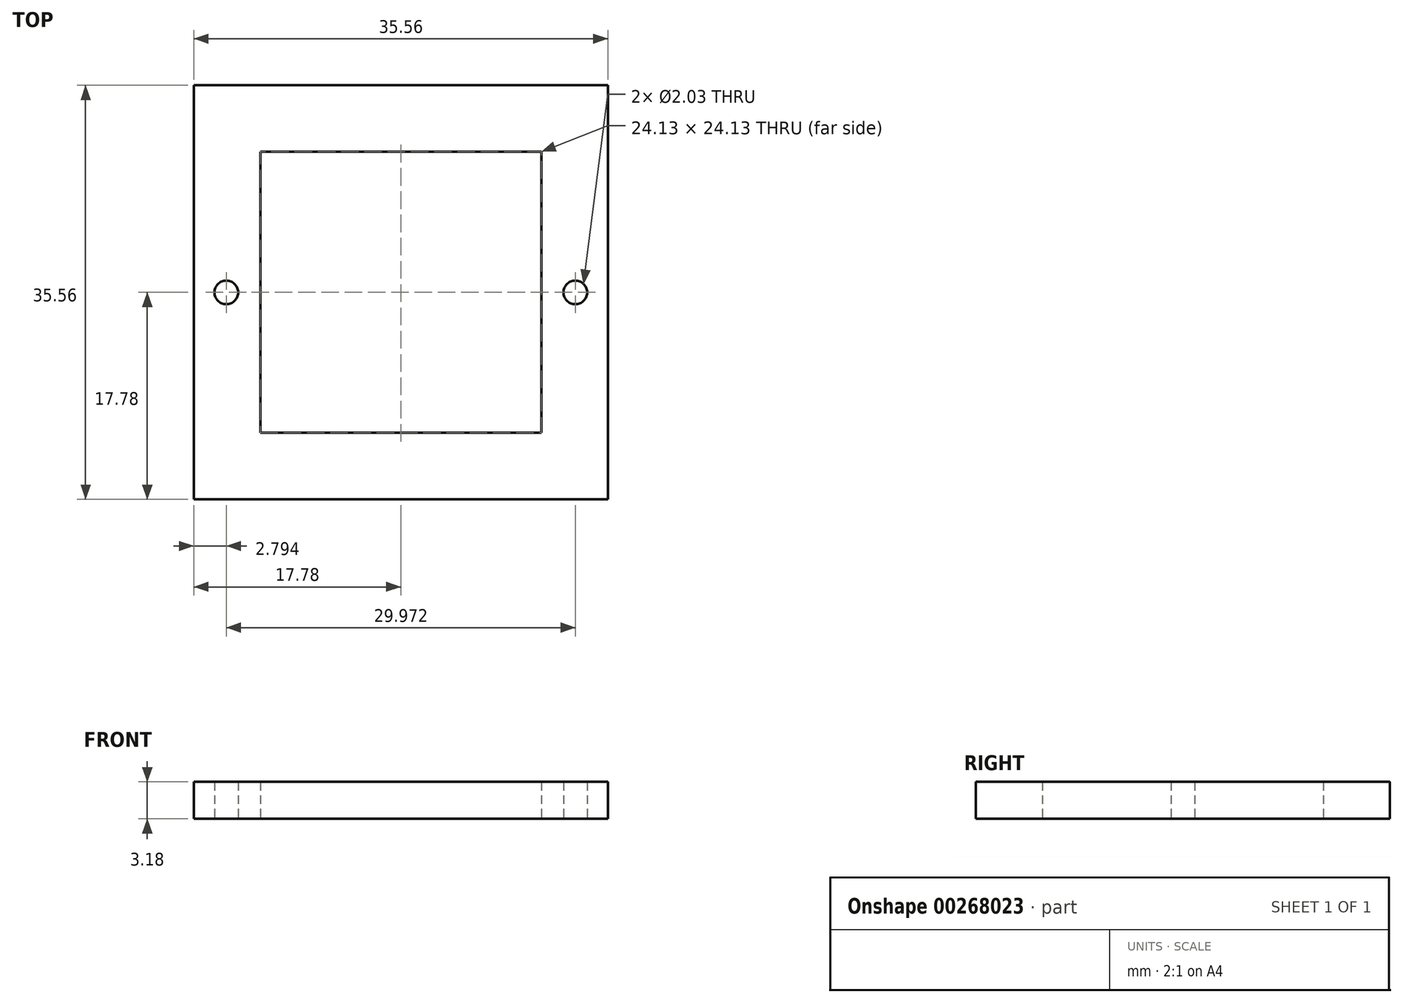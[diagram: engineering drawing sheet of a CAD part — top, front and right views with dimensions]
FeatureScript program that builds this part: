
annotation { "Feature Type Name" : "Feature", "Feature Type Description" : "" }
export const myFeature = defineFeature(function(context is Context, id is Id, definition is map)
    precondition{}
    {
        {
            var Q0;
            Q0=qCreatedBy(makeId("Top.planeOp"),FACE);
            var sketch = newSketch(context, id + "F0", { "sketchPlane" : qUnion([Q0])});
            skLineSegment(sketch, "E0.bottom", {"start": v(12.07, 12.07) * mm, "end": v(-12.07, 12.07) * mm});
            skLineSegment(sketch, "E0.top", {"start": v(12.07, -12.06) * mm, "end": v(-12.07, -12.06) * mm});
            skLineSegment(sketch, "E0.left", {"start": v(12.07, 12.07) * mm, "end": v(12.07, -12.06) * mm});
            skLineSegment(sketch, "E0.right", {"start": v(-12.07, 12.07) * mm, "end": v(-12.07, -12.06) * mm});
            skPoint(sketch, "E0.middle", {"position": v(0, 0) * mm});
            skLineSegment(sketch, "E1.bottom", {"start": v(17.78, 17.78) * mm, "end": v(-17.78, 17.78) * mm});
            skLineSegment(sketch, "E1.top", {"start": v(17.78, -17.78) * mm, "end": v(-17.78, -17.78) * mm});
            skLineSegment(sketch, "E1.left", {"start": v(17.78, 17.78) * mm, "end": v(17.78, -17.78) * mm});
            skLineSegment(sketch, "E1.right", {"start": v(-17.78, 17.78) * mm, "end": v(-17.78, -17.78) * mm});
            skLineSegment(sketch, "E2", {"start": v(-17.78, 0) * mm, "end": v(17.78, 0) * mm, "construction": true});
            skCircle(sketch, "E3", {"center": v(14.99, 0) * mm, "radius": 1.02 * mm});
            skCircle(sketch, "E4", {"center": v(-14.99, 0) * mm, "radius": 1.02 * mm});
            skSolve(sketch);
        }
        {
            var Q0;
            Q0=makeQuery(id+"F0.imprint","IMPRINT",FACE,{"disambiguationData":[TD([[makeQuery(id+"F0.imprint","IMPRINT",EDGE,{"derivedFrom":sQuery(id+"F0.wireOp",EDGE,"E0.bottom")}),-1.0]])]});
            extrude(context, id + "F1", {"entities" : qUnion([Q0]), "depth" : 3.17 * mm});
        }
    });
